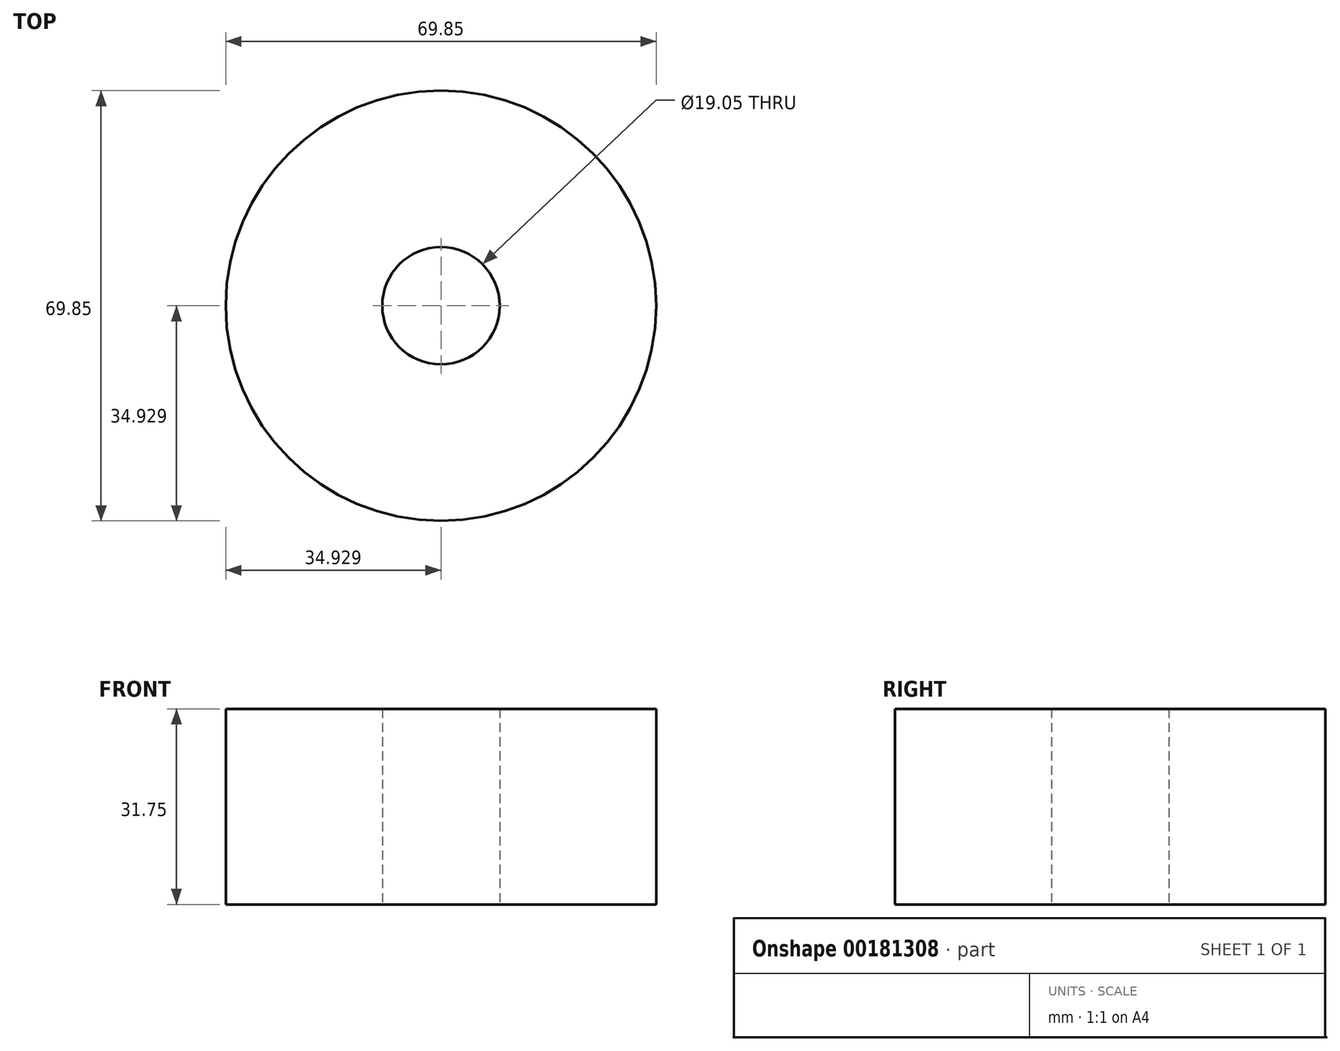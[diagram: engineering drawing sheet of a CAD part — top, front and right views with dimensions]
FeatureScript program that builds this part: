
annotation { "Feature Type Name" : "Feature", "Feature Type Description" : "" }
export const myFeature = defineFeature(function(context is Context, id is Id, definition is map)
    precondition{}
    {
        {
            var Q0;
            Q0=qCreatedBy(makeId("Top.planeOp"),FACE);
            var sketch = newSketch(context, id + "F0", { "sketchPlane" : qUnion([Q0])});
            skCircle(sketch, "E0", {"center": v(0.33, 0.5) * mm, "radius": 34.93 * mm});
            skCircle(sketch, "E1", {"center": v(0.33, 0.5) * mm, "radius": 9.53 * mm});
            skSolve(sketch);
        }
        {
            var Q0;
            Q0 = qSketchRegion(id + "F0", true);
            var Q1;
            Q1=makeQuery(id+"F0.imprint","IMPRINT",FACE,{"disambiguationData":[TD([[makeQuery(id+"F0.imprint","IMPRINT",EDGE,{"derivedFrom":sQuery(id+"F0.wireOp",EDGE,"E0")}),1.0]])]});
            extrude(context, id + "F1", {"entities" : qUnion([Q0, Q1]), "depth" : 31.75 * mm});
        }
    });
